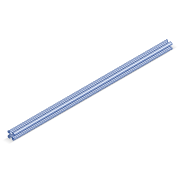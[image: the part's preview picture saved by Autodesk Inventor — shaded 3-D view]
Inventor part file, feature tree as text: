
AUTODESK INVENTOR PART (.ipt)
format: ipt  version: 2020 (Build 240168000, 168)  size: 140,288 bytes
history: mixed  units: in
note: dims shown in document units (in); Inventor stores cm internally (conversion verified against a paired STEP export)
features: fillet x1, imported_body x1
ambient origin geometry x8: Origin, YZ Plane, XZ Plane, XY Plane, X Axis, Y Axis, Z Axis, Center Point
bodies: Solid1 (imported_parasolid)
feature tree (2):
  fillet  "Fillet1"  [1 undecoded]
  imported_body  NMx_Import_Brep_tag  [imported B-rep: ~63 faces, bbox_mm=[20.0, 20.0, 500.0]]
note: 1 required parameter value undecoded (feature->parameter linkage not recoverable at this tier; creation-order binding heuristic only, values carry confidence <= 0.55)
